# Revit family: Building-IEC309Connections-GEWISS-IEC309HP-10°_FLUSH-MOUNT_SOCKET_125A_IP66-67
name_source: partatom
category: Apparecchi elettrici
units: mm (PartAtom-declared; Revit-internal decimal feet)

## family parameters
Condiviso = Sì
Host = Superficie
Mantenere orientamento annotazione = Sì
Punto di calcolo locali = Sì
Quota connettore circolare = Usa diametro
Taglio con vuoti quando caricato = No
Tipo di parte = Normale

## types (26) — shared parameters
BLOCCO = B=C
Breaking capacity at 1.1 Un = 156A
Catalogue = BUILDING
Corpo centrale = Default(2)
Electrocod = 2211
FORMULA = 1000 mm  [stored 3.28084 ft]
Flange dimensions (mm) = 114x114
Glow wire test: = 850 °C (active parts) - 650 °C (passive parts)
IDF = d570d9ae-38ca-4fd7-91b8-255d427c8406
IDT = f8cfd48370014e8f8fb3c269094b72df
Immagine tipo = <Nessuno>
Insulation resistance = - 10 M?
L = 155 mm  [stored 0.50853 ft]
Operating temperature: = -25 +55 °C
Piastra = Default(2)
Produttore = GEWISS S.p.A.
Prospetto di default = 1219 mm
Rated current (A) = 125
SEO = Socket outlet
SPinotto = Default(2)
Sportello_visibile = Sì
Spostamento_S = 943 mm
Technical sheet = https://www.gewiss.com
Terminal tightening capacity = 16-50mm² flexible cables - 25-70mm² rigid cables
Thermo-pressure with ball = 125 °C (active parts) - 80 °C (passive parts)
Total number of operations = -500
Typology = 10° angled flush-mounting socket-outlet
URL = https://www.gewiss.com
Version file RFA = 21.11
W = 115 mm  [stored 0.377297 ft]

## per-type parameters (varying)
| type | Characteristics | Colour: | Cover dimensions mm | Descrizione | Frequency | IP degree | Modello | No. of poles | Rated voltage | Rated voltage: | Reference h | Shock resistance | Type of material | Type of wiring |
| GW62965H - 10°FLUSH.S.O.HP IP67 2P+E 125A 110V 4H |  | Yellow |  | 10°FLUSH.S.O.HP IP67 2P+E 125A 110V 4H | 50/60 Hz | IP66/IP67 | GW62965H | 2P+E |  | 100 - 130 V | 4 | IK09 | Halogen-free in compliance with EN 60754-2 | Mantle terminal |
| GW62261H - 10°FLUSH.S.O.HP IP67 3P+E 125A 400V 6H |  | Red |  | 10°FLUSH.S.O.HP IP67 3P+E 125A 400V 6H | 50/60 Hz | IP66/IP67 | GW62261H | 3P+E |  | 380 - 415 V | 6 | IK09 | Halogen-free in compliance with EN 60754-2 | Mantle terminal |
| GW62975H - 10°FLUSH.S.O.HP IP67 3P+E 125A-50V 2H |  | Green |  | 10°FLUSH.S.O.HP IP67 3P+E 125A >50V 2H | -300 - 500 Hz | IP66/IP67 | GW62975H | 3P+E |  | -50 V | 2 | IK09 | Halogen-free in compliance with EN 60754-2 | Mantle terminal |
| GW62257H - 10°FLUSH.S.O.HP IP67 3P+E 125A 110V 4H |  | Yellow |  | 10°FLUSH.S.O.HP IP67 3P+E 125A 110V 4H | 50/60 Hz | IP66/IP67 | GW62257H | 3P+E |  | 100 - 130 V | 4 | IK09 | Halogen-free in compliance with EN 60754-2 | Mantle terminal |
| GW62976H - 10°FLUSH.S.O.HP IP67 3P+N+E 125A-50V 2H |  | Green |  | 10°FLUSH.S.O.HP IP67 3P+N+E 125A >50V 2H | -300 - 500 Hz | IP66/IP67 | GW62976H | 3P+N+E |  | -50 V | 2 | IK09 | Halogen-free in compliance with EN 60754-2 | Mantle terminal |
| GW62264H - 10°FLUSH.S.O.HP IP67 3P+N+E 125A 500V 7H |  | Black |  | 10°FLUSH.S.O.HP IP67 3P+N+E 125A 500V 7H | 50/60 Hz | IP66/IP67 | GW62264H | 3P+N+E |  | 480 - 500 V | 7 | IK09 | Halogen-free in compliance with EN 60754-2 | Mantle terminal |
| GW62260H - 10°FLUSH.S.O.HP IP67 3P+N+E 125A 230V 9H |  | Blue |  | 10°FLUSH.S.O.HP IP67 3P+N+E 125A 230V 9H | 50/60 Hz | IP66/IP67 | GW62260H | 3P+N+E |  | 200 - 250 V | 9 | IK09 | Halogen-free in compliance with EN 60754-2 | Mantle terminal |
| GW62974H - 10°FLUSH.S.O.HP IP67 2P+E 125A-50V 2H |  | Green |  | 10°FLUSH.S.O.HP IP67 2P+E 125A >50V 2H | -300 - 500 Hz | IP66/IP67 | GW62974H | 2P+E |  | -50 V | 2 | IK09 | Halogen-free in compliance with EN 60754-2 | Mantle terminal |
| GW62259H - 10°FLUSH.S.O.HP IP67 3P+E 125A 230V 9H |  | Blue |  | 10°FLUSH.S.O.HP IP67 3P+E 125A 230V 9H | 50/60 Hz | IP66/IP67 | GW62259H | 3P+E |  | 200 - 250 V | 9 | IK09 | Halogen-free in compliance with EN 60754-2 | Mantle terminal |
| GW62969H - 10°FLUSH.S.O.HP IP67 3P+E 125A 690V 5H |  | Black |  | 10°FLUSH.S.O.HP IP67 3P+E 125A 690V 5H | 50/60 Hz | IP66/IP67 | GW62969H | 3P+E |  | 600 - 690 V | 5 | IK09 | Halogen-free in compliance with EN 60754-2 | Mantle terminal |
| GW62970H - 10°FLUSH.S.O.HP IP67 3P+N+E 125A 690V 5H |  | Black |  | 10°FLUSH.S.O.HP IP67 3P+N+E 125A 690V 5H | 50/60 Hz | IP66/IP67 | GW62970H | 3P+N+E |  | 600 - 690 V | 5 | IK09 | Halogen-free in compliance with EN 60754-2 | Mantle terminal |
| GW62978H - 10°FL.S.O.HP IP67 3P+N+E 125A440÷460V11H |  | Red |  | 10°FL.S.O.HP IP67 3P+N+E 125A440÷460V11H | 60 Hz | IP66/IP67 | GW62978H | 3P+N+E |  | 440 - 460 V | 11 | IK09 | Halogen-free in compliance with EN 60754-2 | Mantle terminal |
| GW62973H - 10°FLUSH.S.O.HP IP67 3P+N+E125A-50V 10H |  | Green |  | 10°FLUSH.S.O.HP IP67 3P+N+E125A >50V 10H | 100 - 300 Hz | IP66/IP67 | GW62973H | 3P+N+E |  | -50 V | 10 | IK09 | Halogen-free in compliance with EN 60754-2 | Mantle terminal |
| GW62966H - 10°FLUSH.S.O.HP IP67 2P+E 125A 230V 6H |  | Blue |  | 10°FLUSH.S.O.HP IP67 2P+E 125A 230V 6H | 50/60 Hz | IP66/IP67 | GW62966H | 2P+E |  | 200 - 250 V | 6 | IK09 | Halogen-free in compliance with EN 60754-2 | Mantle terminal |
| GW68786 - WT. SOCKET 125A 3P+N+E 400V AUX. CONT. |  | Red | 114x114 | WT. SOCKET 125A 3P+N+E 400V AUX. CONT. | 50/60 Hz | IP67 | GW68786 | 3P+N+E | 380-415V |  | 6 | IK08 |  | With screw |
| GW62263H - 10°FLUSH.S.O.HP IP67 3P+E 125A 500V 7H |  | Black |  | 10°FLUSH.S.O.HP IP67 3P+E 125A 500V 7H | 50/60 Hz | IP66/IP67 | GW62263H | 3P+E |  | 480 - 500 V | 7 | IK09 | Halogen-free in compliance with EN 60754-2 | Mantle terminal |
| GW62968H - 10°FLUSH.S.O.HP IP67 2P+E 125A 500V 7H |  | Black |  | 10°FLUSH.S.O.HP IP67 2P+E 125A 500V 7H | 50/60 Hz | IP66/IP67 | GW62968H | 2P+E |  | 480 - 500 V | 7 | IK09 | Halogen-free in compliance with EN 60754-2 | Mantle terminal |
| GW62262PH - 10°FL.S.O.HP IP67 3P+N+E 125A 400V6H PC | Pilot contact | Red |  | 10°FL.S.O.HP IP67 3P+N+E 125A 400V6H PC | 50/60 Hz | IP66/IP67 | GW62262PH | 3P+N+E |  | 346 - 415 V | 6 | IK09 | Halogen-free in compliance with EN 60754-2 | Mantle terminal |
| GW62971H - 10°FLUSH.S.O.HP IP67 2P+E 125A-50V 10H |  | Green |  | 10°FLUSH.S.O.HP IP67 2P+E 125A >50V 10H | 100 - 300 Hz | IP66/IP67 | GW62971H | 2P+E |  | -50 V | 10 | IK09 | Halogen-free in compliance with EN 60754-2 | Mantle terminal |
| GW62977H - 10°FL.S.O.HP IP67 3P+E 125A 440÷460V11H |  | Red |  | 10°FL.S.O.HP IP67 3P+E 125A 440÷460V11H | 60 Hz | IP66/IP67 | GW62977H | 3P+E |  | 440 - 460 V | 11 | IK09 | Halogen-free in compliance with EN 60754-2 | Mantle terminal |
| GW62972H - 10°FLUSH.S.O.HP IP67 3P+E 125A-50V 10H |  | Green |  | 10°FLUSH.S.O.HP IP67 3P+E 125A >50V 10H | 100 - 300 Hz | IP66/IP67 | GW62972H | 3P+E |  | -50 V | 10 | IK09 | Halogen-free in compliance with EN 60754-2 | Mantle terminal |
| GW68785 - WT. SOCKET 125A 3P+E 400V AUX. CONT. |  | Red | 114x114 | WT. SOCKET 125A 3P+E 400V AUX. CONT. | 50/60 Hz | IP67 | GW68785 | 3P+E | 380-415V |  | 6 | IK08 |  | With screw |
| GW62967H - 10°FLUSH.S.O.HP IP67 2P+E 125A 400V 9H |  | Red |  | 10°FLUSH.S.O.HP IP67 2P+E 125A 400V 9H | 50/60 Hz | IP66/IP67 | GW62967H | 2P+E |  | 380 - 415 V | 9 | IK09 | Halogen-free in compliance with EN 60754-2 | Mantle terminal |
| GW62258H - 10°FLUSH.S.O.HP IP67 3P+N+E 125A 110V 4H |  | Yellow |  | 10°FLUSH.S.O.HP IP67 3P+N+E 125A 110V 4H | 50/60 Hz | IP66/IP67 | GW62258H | 3P+N+E |  | 100 - 130 V | 4 | IK09 | Halogen-free in compliance with EN 60754-2 | Mantle terminal |
| GW62261PH - 10°FLUSH.S.O.HP IP67 3P+E 125A 400V6H PC | Pilot contact | Red |  | 10°FLUSH.S.O.HP IP67 3P+E 125A 400V6H PC | 50/60 Hz | IP66/IP67 | GW62261PH | 3P+E |  | 380 - 415 V | 6 | IK09 | Halogen-free in compliance with EN 60754-2 | Mantle terminal |
| GW62262H - 10°FLUSH.S.O.HP IP67 3P+N+E 125A 400V 6H |  | Red |  | 10°FLUSH.S.O.HP IP67 3P+N+E 125A 400V 6H | 50/60 Hz | IP66/IP67 | GW62262H | 3P+N+E |  | 346 - 415 V | 6 | IK09 | Halogen-free in compliance with EN 60754-2 | Mantle terminal |

note: [stored X ft] marks values corroborated as IEEE doubles in the binary element streams (Revit-internal decimal feet)

## geometry (parser evidence)
native form markers: Sweep x2
no freeform markers — native parametric forms only
